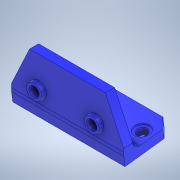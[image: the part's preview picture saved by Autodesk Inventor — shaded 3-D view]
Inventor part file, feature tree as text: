
AUTODESK INVENTOR PART (.ipt)
format: ipt  version: 2022.6 (Build 266554000, 554)  size: 226,304 bytes
history: native  units: mm
features: sketch x6, projected_geometry x3, extrude x2, hole x2, chamfer x2, other x1, rib x1, fillet x1
ambient origin geometry x8: Origin, YZ Plane, XZ Plane, XY Plane, X Axis, Y Axis, Z Axis, Center Point
bodies: Solid1 (feature_tree)
feature tree (18):
  extrude  "Extrusion1"  Depth=3.0mm
  hole  "mounting holes"  [1 undecoded]
  sketch  "Sketch4"  dims[d16=6.5mm]
  chamfer  "Chamfer3"  Distance=37.0mm
  chamfer  "Chamfer4"  Distance=2.0mm Angle=45.0deg
  hole  "Hole4"  [1 undecoded]
  extrude  "Extrusion5"  Depth=2.0mm
  other  "Bend Part2"
  rib  "Rib3"
  fillet  "Fillet4"  Radius=5.0mm
  sketch  "Sketch1"  dims[d0=3.0mm d1=3.0mm]
  sketch  "Sketch3"  dims[d2=16.0mm d3=18.0mm d4=37.0mm d5=0.0mm]
  projected_geometry  "Projected Loop1"
  sketch  "Sketch12"  dims[d17=30.0mm]
  projected_geometry  "Projected Loop7"
  sketch  "Sketch13"  dims[d18=3.4mm d19=6.0mm d20=5.0mm d21=0.5mm d22=90.0deg d23=8.0mm d24=20.594885mm]
  projected_geometry  "Projected Loop8"
  sketch  "Sketch14"  dims[d31=1.0mm d69=3.0mm d70=2.0mm d71=45.0deg d72=6.0mm d73=2.0mm d74=11.34464mm d84=19.0mm d85=5.0mm d86=3.4mm d87=6.0mm d88=5.0mm d89=0.5mm d90=90.0deg d91=8.0mm d92=20.594885mm d93=5.0mm d94=5.0mm d95=1.5mm d96=0.0mm d97=7.0mm d98=1.22173mm d102=1.0mm d103=2.0mm d104=0.0mm d105=0.0mm d106=1.0mm d107=1.0mm d108=8.0mm d109=6.108652mm d110=2.0mm]
note: 2 required parameter values undecoded (feature->parameter linkage not recoverable at this tier; creation-order binding heuristic only, values carry confidence <= 0.55)
